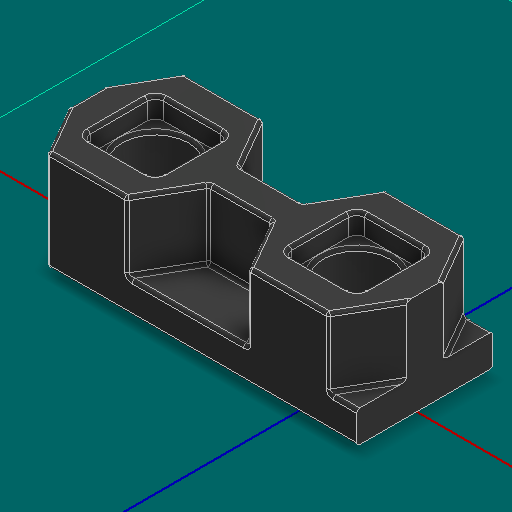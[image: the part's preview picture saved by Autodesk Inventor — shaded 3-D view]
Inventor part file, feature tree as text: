
AUTODESK INVENTOR PART (.ipt)
format: ipt  version: 2025 (Build 290162000, 162)  size: 363,008 bytes
history: native  units: in
note: dims shown in document units (in); Inventor stores cm internally (conversion verified against a paired STEP export)
features: extrude x2, fillet x1, sketch x1
ambient origin geometry x8: Origin, YZ Plane, XZ Plane, XY Plane, X Axis, Y Axis, Z Axis, Center Point
bodies: Solid1 (feature_tree)
feature tree (4):
  fillet  "Fillet6"  Radius=0.0394in
  extrude  "Extrusion1"  [1 undecoded]
  extrude  "Extrusion2"  [1 undecoded]
  sketch  "Sketch2"  dims[d2=0.5in d3=0.0in]
note: 2 required parameter values undecoded (feature->parameter linkage not recoverable at this tier; creation-order binding heuristic only, values carry confidence <= 0.55)
